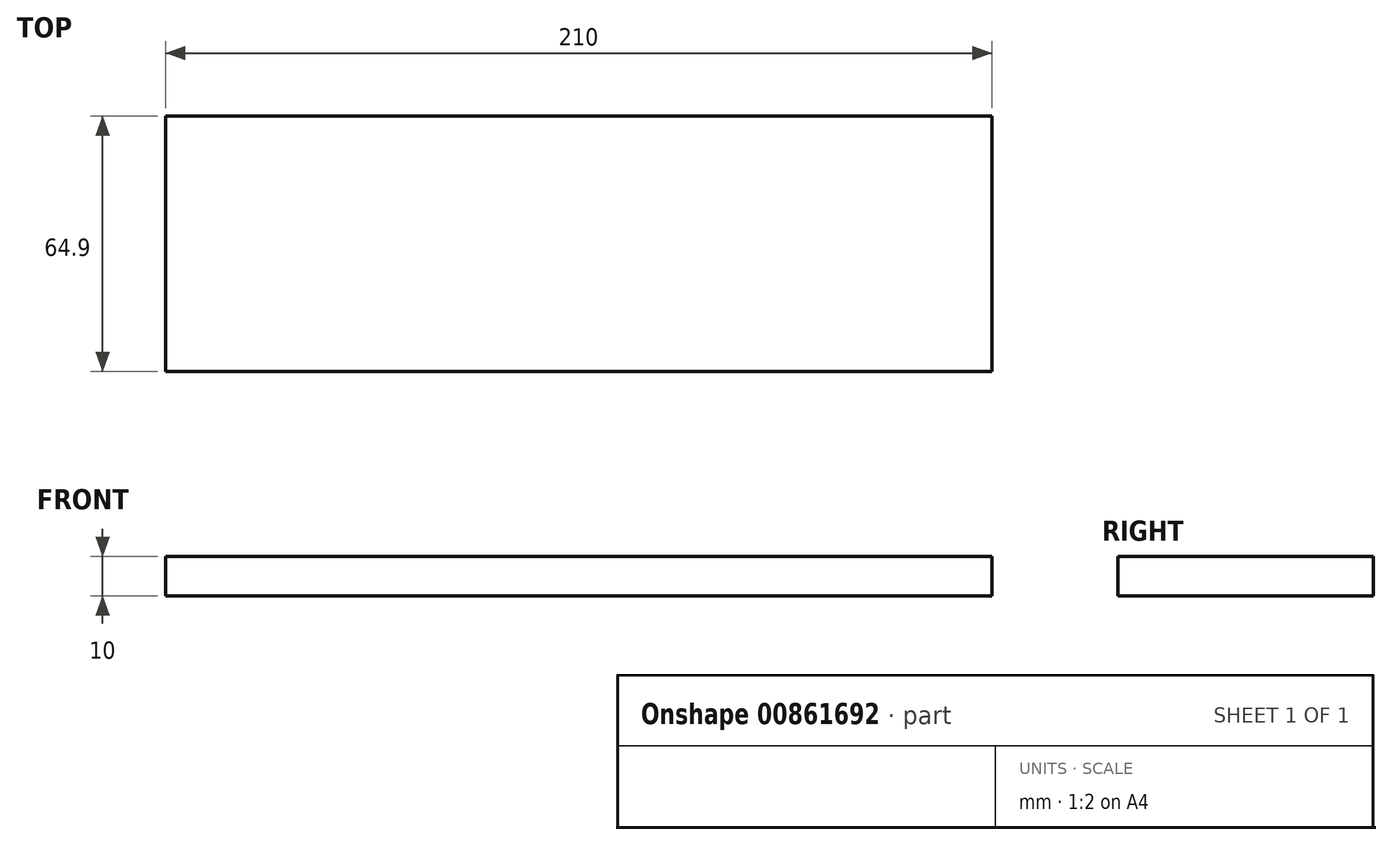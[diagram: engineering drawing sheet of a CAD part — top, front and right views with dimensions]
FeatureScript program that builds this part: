
annotation { "Feature Type Name" : "Feature", "Feature Type Description" : "" }
export const myFeature = defineFeature(function(context is Context, id is Id, definition is map)
    precondition{}
    {
        {
            var Q0;
            Q0=qCreatedBy(makeId("Top.planeOp"),FACE);
            var sketch = newSketch(context, id + "F0", { "sketchPlane" : qUnion([Q0])});
            skLineSegment(sketch, "E0.bottom", {"start": v(105, -32.45) * mm, "end": v(-105, -32.45) * mm});
            skLineSegment(sketch, "E0.top", {"start": v(105, 32.45) * mm, "end": v(-105, 32.45) * mm});
            skLineSegment(sketch, "E0.left", {"start": v(105, -32.45) * mm, "end": v(105, 32.45) * mm});
            skLineSegment(sketch, "E0.right", {"start": v(-105, -32.45) * mm, "end": v(-105, 32.45) * mm});
            skPoint(sketch, "E0.middle", {"position": v(0, 0) * mm});
            skSolve(sketch);
        }
        {
            var Q0;
            Q0 = qSketchRegion(id + "F0", true);
            extrude(context, id + "F1", {"entities" : qUnion([Q0]), "depth" : 10 * mm, "offsetDistance" : 25 * mm});
        }
    });
